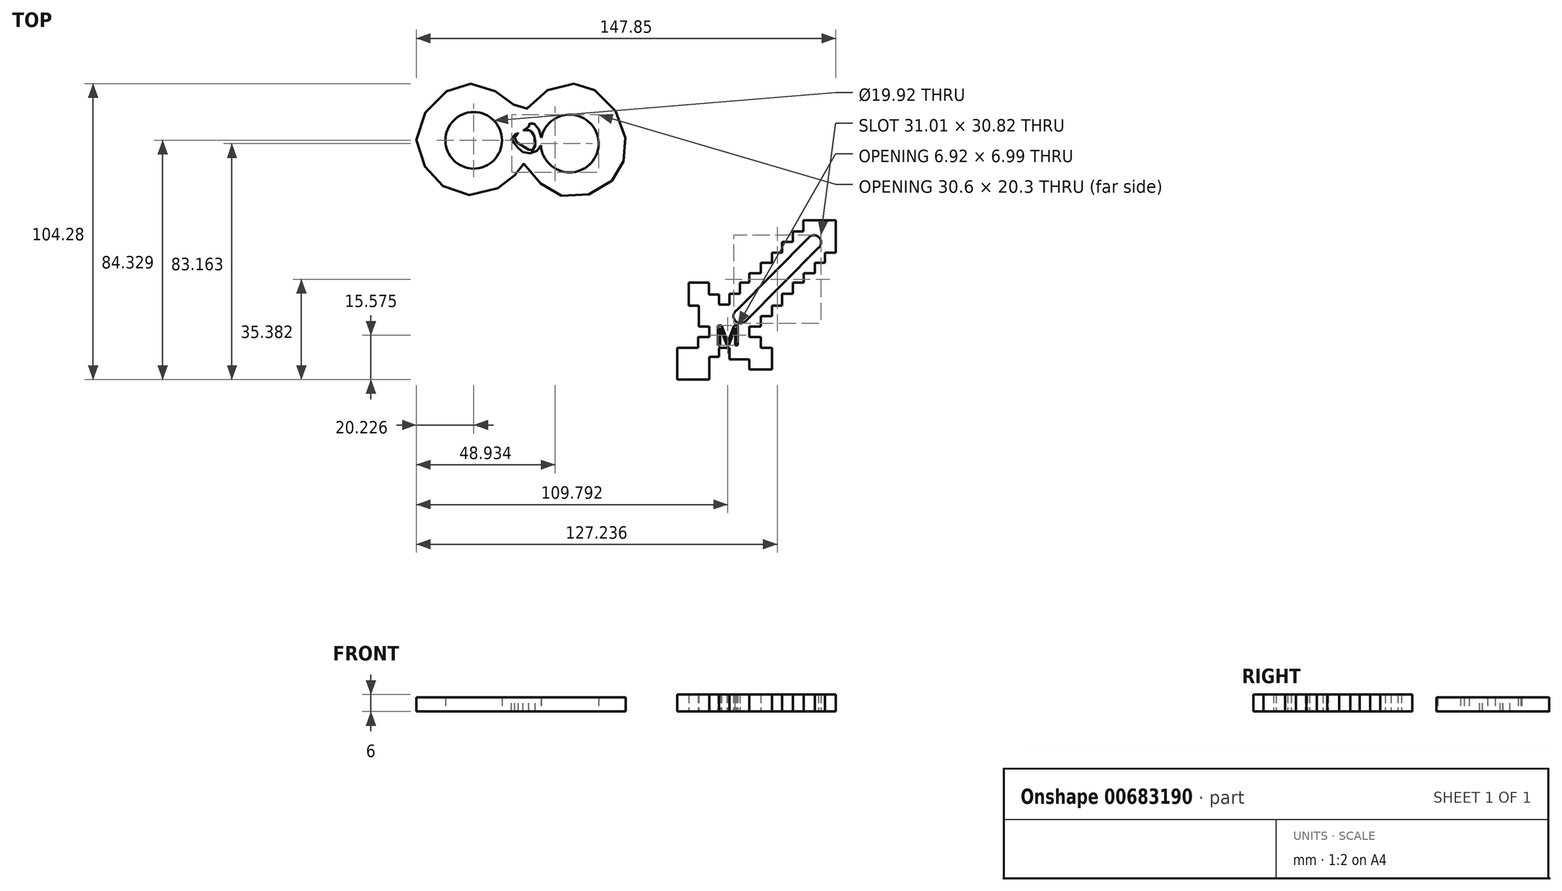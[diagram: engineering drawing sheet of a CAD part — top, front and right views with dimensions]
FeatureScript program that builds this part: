
annotation { "Feature Type Name" : "Feature", "Feature Type Description" : "" }
export const myFeature = defineFeature(function(context is Context, id is Id, definition is map)
    precondition{}
    {
        {
            var Q0;
            Q0=qCreatedBy(makeId("Top.planeOp"),FACE);
            var sketch = newSketch(context, id + "F0", { "sketchPlane" : qUnion([Q0])});
            skFitSpline(sketch, "E0", {"points": [v(-42.92, 37.3) * mm, v(-49.51, 42.18) * mm, v(-59.29, 44.7) * mm, v(-69.13, 40.03) * mm, v(-76.9, 28.2) * mm, v(-74.57, 16.3) * mm, v(-66.87, 8.1) * mm, v(-54.92, 5.7) * mm, v(-44.19, 10.58) * mm, v(-41.61, 13.93) * mm, v(-39.56, 16.55) * mm, v(-32.64, 8.8) * mm, v(-24.46, 5) * mm, v(-12.4, 7.21) * mm, v(-5.6, 14.17) * mm, v(-3.44, 21.33) * mm, v(-5.3, 32.25) * mm, v(-14.41, 42.56) * mm, v(-21.65, 44.7) * mm, v(-32.83, 41.22) * mm, v(-39.75, 35.05) * mm, v(-42.92, 37.3) * mm]});
            skCircle(sketch, "E1", {"center": v(-23.1, 23.65) * mm, "radius": 10.2 * mm});
            skCircle(sketch, "E2", {"center": v(-56.94, 24.77) * mm, "radius": 9.96 * mm});
            skFitSpline(sketch, "E3", {"points": [v(-33.1, 25.64) * mm, v(-36, 30.75) * mm, v(-37.5, 30.38) * mm, v(-37.69, 29.26) * mm, v(-39.56, 28.32) * mm, v(-36.94, 28.13) * mm, v(-35.45, 22.53) * mm, v(-36.75, 21.22) * mm, v(-39.56, 22.71) * mm, v(-42.55, 25.52) * mm, v(-41.24, 27.39) * mm, v(-43.48, 25.7) * mm, v(-42.55, 23.65) * mm, v(-39.56, 20.66) * mm, v(-34.7, 21.03) * mm, v(-33.1, 25.64) * mm]});
            skSolve(sketch);
        }
        {
            var Q0;
            Q0 = qSketchRegion(id + "F0", true);
            extrude(context, id + "F1", {"entities" : qUnion([Q0]), "depth" : 5 * mm, "offsetDistance" : 25 * mm});
        }
        {
            var Q0;
            Q0=sQuery(id+"F0.wireOp",EDGE,"E3");
            extrude(context, id + "F2", {"bodyType" : ToolBodyType.SURFACE, "surfaceEntities" : qUnion([Q0]), "depth" : 8 * mm, "offsetDistance" : 25 * mm});
        }
        {
            var Q0;
            Q0=qCreatedBy(makeId("Top.planeOp"),FACE);
            var sketch = newSketch(context, id + "F3", { "sketchPlane" : qUnion([Q0])});
            skLineSegment(sketch, "E4", {"start": v(14.74, -59.56) * mm, "end": v(14.74, -48.37) * mm});
            skLineSegment(sketch, "E5", {"start": v(14.74, -48.37) * mm, "end": v(22.15, -48.37) * mm});
            skLineSegment(sketch, "E6", {"start": v(22.15, -48.37) * mm, "end": v(22.15, -44.6) * mm});
            skLineSegment(sketch, "E7", {"start": v(22.15, -44.6) * mm, "end": v(26.07, -44.6) * mm});
            skLineSegment(sketch, "E8", {"start": v(26.07, -44.6) * mm, "end": v(26.07, -40.82) * mm});
            skLineSegment(sketch, "E9", {"start": v(26.07, -40.82) * mm, "end": v(22.44, -40.82) * mm});
            skLineSegment(sketch, "E10", {"start": v(22.44, -40.82) * mm, "end": v(22.44, -33.55) * mm});
            skLineSegment(sketch, "E11", {"start": v(22.44, -33.55) * mm, "end": v(18.8, -33.55) * mm});
            skLineSegment(sketch, "E12", {"start": v(18.8, -33.55) * mm, "end": v(18.8, -25.41) * mm});
            skLineSegment(sketch, "E13", {"start": v(18.8, -25.41) * mm, "end": v(25.93, -25.41) * mm});
            skLineSegment(sketch, "E14", {"start": v(25.93, -25.41) * mm, "end": v(25.93, -29.63) * mm});
            skLineSegment(sketch, "E15", {"start": v(25.93, -29.63) * mm, "end": v(29.56, -29.63) * mm});
            skLineSegment(sketch, "E16", {"start": v(29.56, -29.63) * mm, "end": v(29.56, -33.12) * mm});
            skLineSegment(sketch, "E17", {"start": v(29.56, -33.12) * mm, "end": v(33.2, -33.12) * mm});
            skLineSegment(sketch, "E18", {"start": v(33.2, -33.12) * mm, "end": v(33.2, -29.34) * mm});
            skLineSegment(sketch, "E19", {"start": v(33.2, -29.34) * mm, "end": v(36.83, -29.34) * mm});
            skLineSegment(sketch, "E20", {"start": v(36.83, -29.34) * mm, "end": v(36.83, -25.41) * mm});
            skLineSegment(sketch, "E21", {"start": v(36.83, -25.41) * mm, "end": v(40.17, -25.41) * mm});
            skLineSegment(sketch, "E22", {"start": v(40.17, -25.41) * mm, "end": v(40.17, -22.07) * mm});
            skLineSegment(sketch, "E23", {"start": v(40.17, -22.07) * mm, "end": v(44.24, -22.07) * mm});
            skLineSegment(sketch, "E24", {"start": v(44.24, -22.07) * mm, "end": v(44.24, -18.44) * mm});
            skLineSegment(sketch, "E25", {"start": v(44.24, -18.44) * mm, "end": v(48.16, -18.44) * mm});
            skLineSegment(sketch, "E26", {"start": v(48.16, -18.44) * mm, "end": v(48.16, -14.8) * mm});
            skLineSegment(sketch, "E27", {"start": v(48.16, -14.8) * mm, "end": v(51.8, -14.8) * mm});
            skLineSegment(sketch, "E28", {"start": v(51.8, -14.8) * mm, "end": v(51.8, -11.03) * mm});
            skLineSegment(sketch, "E29", {"start": v(51.8, -11.03) * mm, "end": v(55.57, -11.03) * mm});
            skLineSegment(sketch, "E30", {"start": v(55.57, -11.03) * mm, "end": v(55.57, -7.4) * mm});
            skLineSegment(sketch, "E31", {"start": v(55.57, -7.4) * mm, "end": v(59.2, -7.4) * mm});
            skLineSegment(sketch, "E32", {"start": v(59.2, -7.4) * mm, "end": v(59.2, -3.47) * mm});
            skLineSegment(sketch, "E33", {"start": v(59.2, -3.47) * mm, "end": v(70.68, -3.47) * mm});
            skLineSegment(sketch, "E34", {"start": v(70.68, -3.47) * mm, "end": v(70.68, -14.8) * mm});
            skLineSegment(sketch, "E35", {"start": v(70.68, -14.8) * mm, "end": v(66.9, -14.8) * mm});
            skLineSegment(sketch, "E36", {"start": v(66.9, -14.8) * mm, "end": v(66.9, -18.44) * mm});
            skLineSegment(sketch, "E37", {"start": v(66.9, -18.44) * mm, "end": v(63.27, -18.44) * mm});
            skLineSegment(sketch, "E38", {"start": v(63.27, -18.44) * mm, "end": v(63.27, -22.07) * mm});
            skLineSegment(sketch, "E39", {"start": v(63.27, -22.07) * mm, "end": v(59.35, -22.07) * mm});
            skLineSegment(sketch, "E40", {"start": v(59.35, -22.07) * mm, "end": v(59.35, -25.41) * mm});
            skLineSegment(sketch, "E41", {"start": v(59.35, -25.41) * mm, "end": v(55.57, -25.41) * mm});
            skLineSegment(sketch, "E42", {"start": v(55.57, -25.41) * mm, "end": v(55.57, -29.34) * mm});
            skLineSegment(sketch, "E43", {"start": v(55.57, -29.34) * mm, "end": v(51.8, -29.34) * mm});
            skLineSegment(sketch, "E44", {"start": v(51.8, -29.34) * mm, "end": v(51.8, -33.55) * mm});
            skLineSegment(sketch, "E45", {"start": v(51.8, -33.55) * mm, "end": v(48.16, -33.55) * mm});
            skLineSegment(sketch, "E46", {"start": v(48.16, -33.55) * mm, "end": v(48.16, -37.19) * mm});
            skPoint(sketch, "E46.endSnap0", {"position": v(22.44, -37.19) * mm});
            skLineSegment(sketch, "E47", {"start": v(48.16, -37.19) * mm, "end": v(44.24, -37.19) * mm});
            skLineSegment(sketch, "E48", {"start": v(44.24, -37.19) * mm, "end": v(44.24, -40.82) * mm});
            skLineSegment(sketch, "E49", {"start": v(44.24, -40.82) * mm, "end": v(40.17, -40.82) * mm});
            skLineSegment(sketch, "E50", {"start": v(40.17, -40.82) * mm, "end": v(40.17, -44.6) * mm});
            skLineSegment(sketch, "E51", {"start": v(40.17, -44.6) * mm, "end": v(44.24, -44.6) * mm});
            skLineSegment(sketch, "E52", {"start": v(44.24, -44.6) * mm, "end": v(44.24, -48.37) * mm});
            skLineSegment(sketch, "E53", {"start": v(44.24, -48.37) * mm, "end": v(48.16, -48.37) * mm});
            skLineSegment(sketch, "E54", {"start": v(48.16, -48.37) * mm, "end": v(48.16, -55.93) * mm});
            skLineSegment(sketch, "E55", {"start": v(48.16, -55.93) * mm, "end": v(40.17, -55.93) * mm});
            skLineSegment(sketch, "E56", {"start": v(40.17, -55.93) * mm, "end": v(40.17, -52.44) * mm});
            skLineSegment(sketch, "E57", {"start": v(40.17, -52.44) * mm, "end": v(33.2, -52.44) * mm});
            skLineSegment(sketch, "E58", {"start": v(33.2, -52.44) * mm, "end": v(33.2, -48.37) * mm});
            skLineSegment(sketch, "E59", {"start": v(33.2, -48.37) * mm, "end": v(29.56, -48.37) * mm});
            skLineSegment(sketch, "E60", {"start": v(29.56, -48.37) * mm, "end": v(29.56, -51.57) * mm});
            skLineSegment(sketch, "E61", {"start": v(29.56, -51.57) * mm, "end": v(26.07, -51.57) * mm});
            skLineSegment(sketch, "E62", {"start": v(26.07, -51.57) * mm, "end": v(26.07, -59.56) * mm});
            skLineSegment(sketch, "E63", {"start": v(26.07, -59.56) * mm, "end": v(14.74, -59.56) * mm});
            skCircle(sketch, "E64", {"center": v(62.98, -11.17) * mm, "radius": 2.5 * mm});
            skCircle(sketch, "E65", {"center": v(37.12, -37.19) * mm, "radius": 2.5 * mm});
            skLineSegment(sketch, "E66", {"start": v(34.98, -35.9) * mm, "end": v(61.2, -9.42) * mm});
            skLineSegment(sketch, "E67", {"start": v(64.95, -12.72) * mm, "end": v(38.9, -38.95) * mm});
            skPoint(sketch, "E67.startSnap0", {"position": v(64.95, -3.47) * mm});
            skText(sketch, "E68", { "text": "M Kean\n", "fontName": "OpenSans-Regular.ttf"});
            skText(sketch, "E69", { "text": "M\n", "fontName": "OpenSans-Regular.ttf"});
            const initialGuessF3  = {"E68": [0.04817, -0.0467, 1, 0, 0.00666], "E69": [0.0282, -0.04748, 1, 0, 0.00705]};
            skSetInitialGuess(sketch, initialGuessF3);
            skSolve(sketch);
        }
        {
            var Q0;
            Q0=makeQuery(id+"F3.imprint","IMPRINT",FACE,{"disambiguationData":[TD([[makeQuery(id+"F3.imprint","IMPRINT",EDGE,{"derivedFrom":sQuery(id+"F3.wireOp",EDGE,"E4")}),-1.0]])]});
            extrude(context, id + "F4", {"entities" : qUnion([Q0]), "depth" : 6 * mm, "offsetDistance" : 25 * mm});
        }
    });
